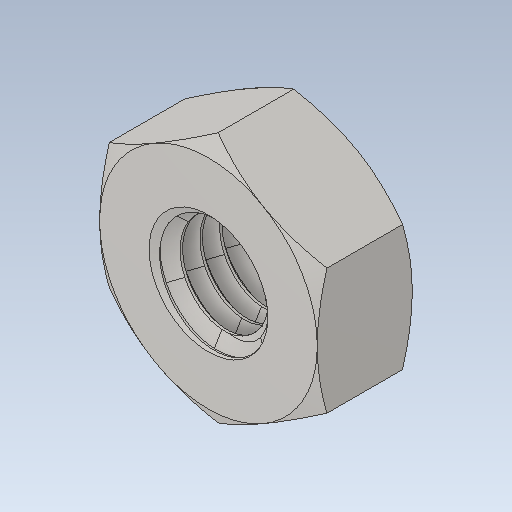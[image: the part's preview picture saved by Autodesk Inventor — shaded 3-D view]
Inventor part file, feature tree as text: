
AUTODESK INVENTOR PART (.ipt)
format: ipt  version: 2020.2 (Build 242310000, 310)  size: 445,440 bytes
history: imported  units: mm
features: imported_body x1
ambient origin geometry x8: Origin, YZ Plane, XZ Plane, XY Plane, X Axis, Y Axis, Z Axis, Center Point
bodies: Solide1 (imported_parasolid), Body1 (imported_parasolid)
feature tree (1):
  imported_body  NMx_Import_Brep_tag  [imported B-rep: ~3 faces, bbox_mm=None]
